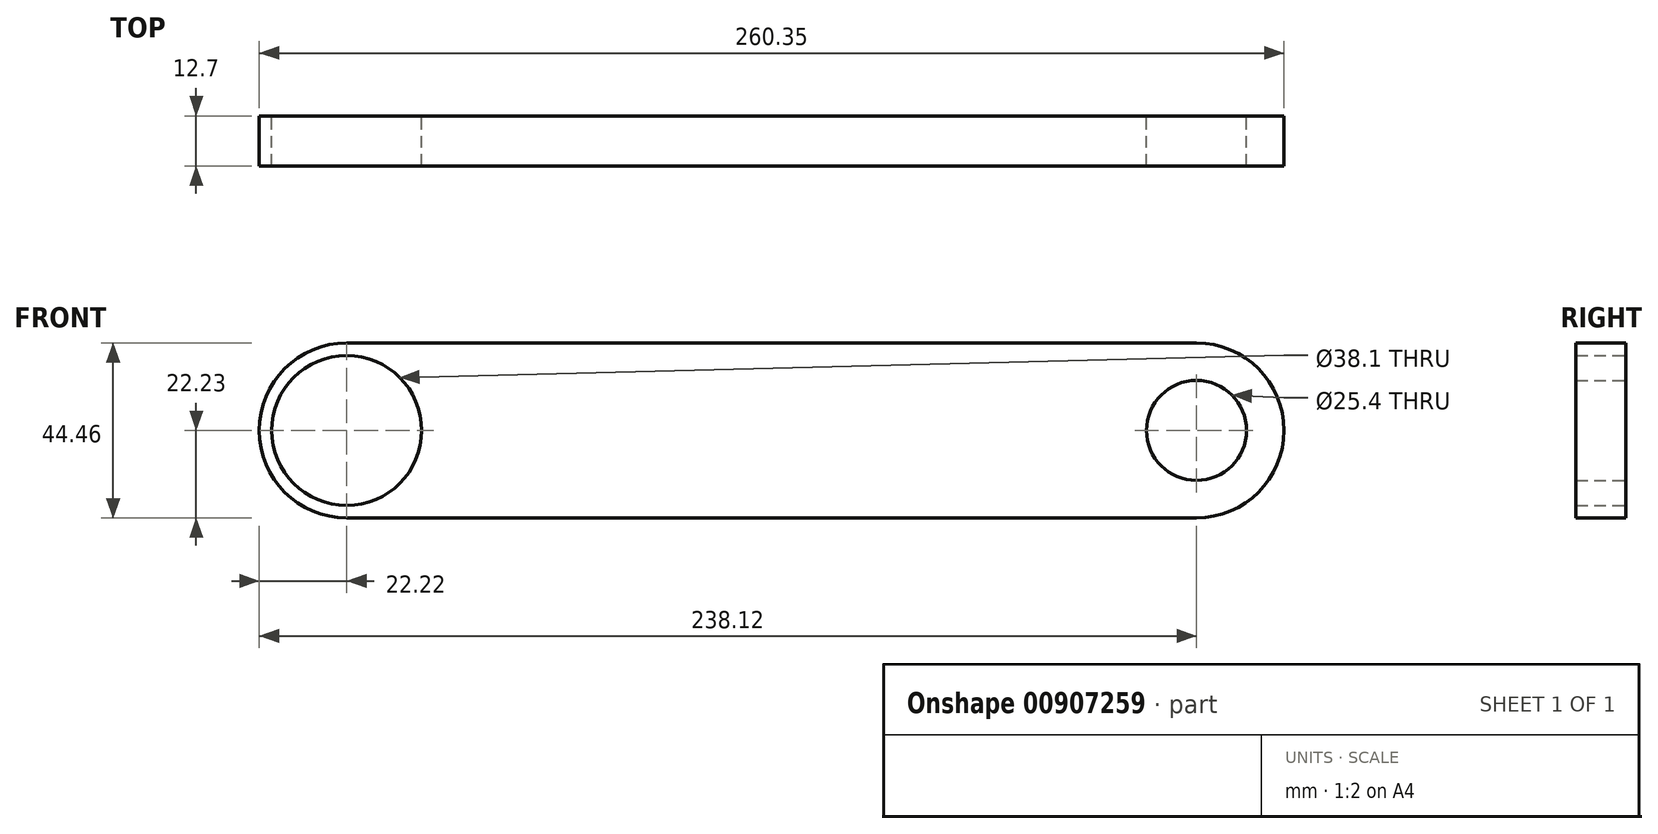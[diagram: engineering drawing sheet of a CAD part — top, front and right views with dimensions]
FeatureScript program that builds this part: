
annotation { "Feature Type Name" : "Feature", "Feature Type Description" : "" }
export const myFeature = defineFeature(function(context is Context, id is Id, definition is map)
    precondition{}
    {
        {
            var Q0;
            Q0=qCreatedBy(makeId("Front.planeOp"),FACE);
            var sketch = newSketch(context, id + "F0", { "sketchPlane" : qUnion([Q0])});
            skLineSegment(sketch, "E0.bottom", {"start": v(107.95, -22.23) * mm, "end": v(-107.95, -22.23) * mm});
            skLineSegment(sketch, "E0.top", {"start": v(107.95, 22.22) * mm, "end": v(-107.95, 22.22) * mm});
            skPoint(sketch, "E0.middle", {"position": v(0, 0) * mm});
            skArc(sketch, "E1", {"start": v(-107.95, 22.22) * mm, "mid": v(-130.17, 0) * mm, "end": v(-107.95, -22.22) * mm});
            skArc(sketch, "E2", {"start": v(107.95, 22.23) * mm, "mid": v(130.18, 0) * mm, "end": v(107.95, -22.22) * mm});
            skCircle(sketch, "E3", {"center": v(-107.95, 0) * mm, "radius": 19.05 * mm});
            skCircle(sketch, "E4", {"center": v(107.95, 0) * mm, "radius": 12.7 * mm});
            skSolve(sketch);
        }
        {
            var Q0;
            Q0=makeQuery(id+"F0.imprint","IMPRINT",FACE,{"disambiguationData":[TD([[makeQuery(id+"F0.imprint","IMPRINT",EDGE,{"derivedFrom":sQuery(id+"F0.wireOp",EDGE,"E0.bottom")}),-1.0]])]});
            extrude(context, id + "F1", {"entities" : qUnion([Q0]), "depth" : 12.7 * mm, "offsetDistance" : 25.4 * mm});
        }
    });
